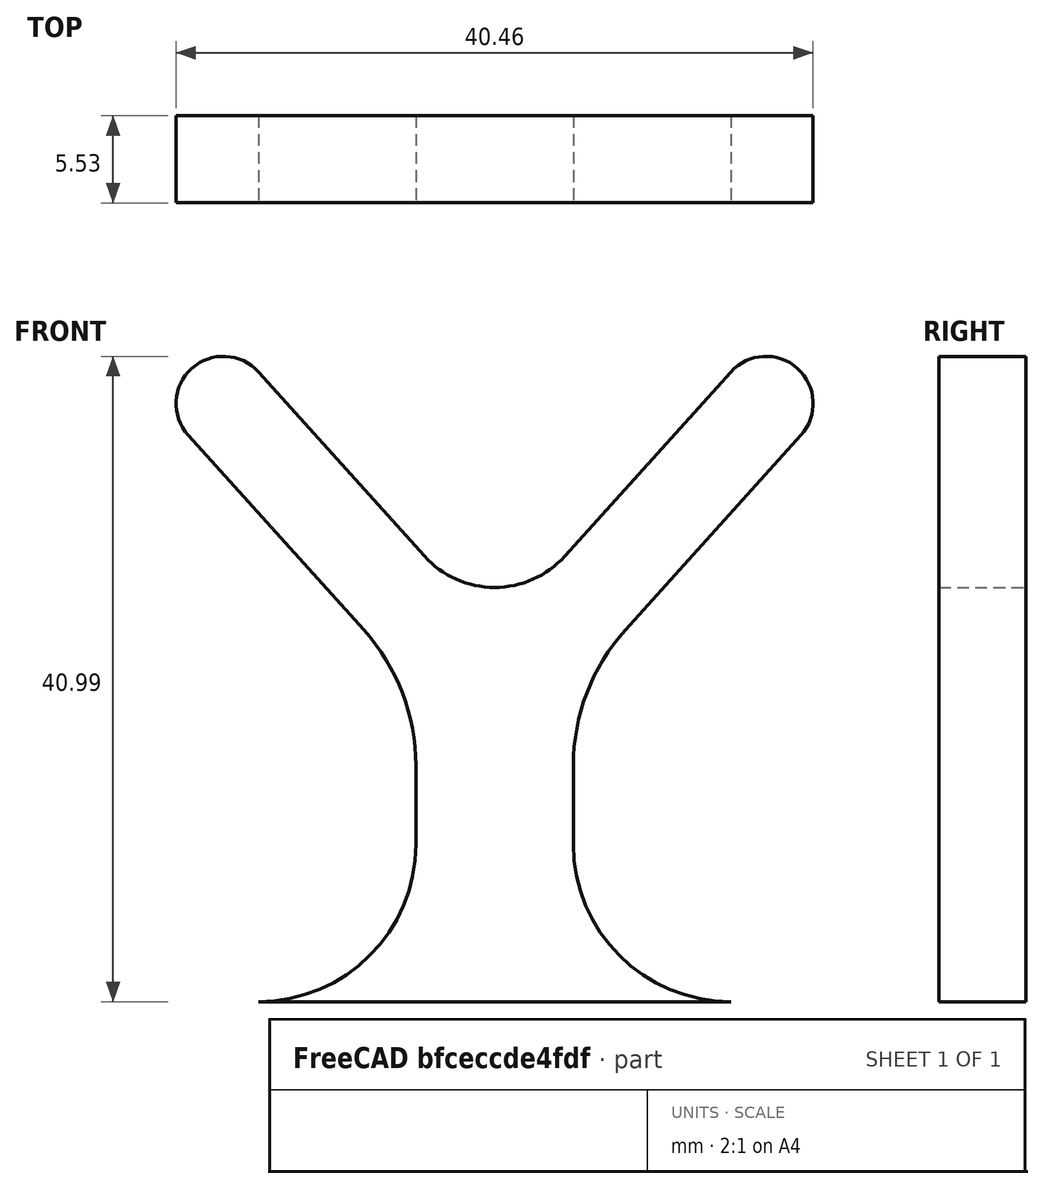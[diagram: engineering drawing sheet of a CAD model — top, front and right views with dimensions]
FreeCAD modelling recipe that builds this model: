
FCSTD DOCUMENT  (FreeCAD 0.15R4537 (Git))
Label: FrontalY_prueba
License: All rights reserved
LicenseURL: http://en.wikipedia.org/wiki/All_rights_reserved
objects: Part::Feature×3, Mesh::Feature×1, Sketcher::SketchObject×1, PartDesign::Pad×1
note: 6 computed .brp shape members not serialized (recipe doc carries the construction recipe); baked Part::Feature solids carry a one-line shape summary decoded from their .brp

FEATURE [Mesh::Feature] G004160_Cycl_marcoFrontalY
FEATURE [Part::Feature] G004160_Cycl_marcoFrontalY001
  shape: bbox 102.5 x 46.5 x 27.49 mm, 3139 faces, 0 solids (baked)
FEATURE [Part::Feature] G004160_Cycl_marcoFrontalY001001  label="G004160_Cycl_marcoFrontalY002"
  shape: bbox 102.5 x 46.5 x 27.49 mm, 1152 faces, 0 solids (baked)
FEATURE [Part::Feature] G004160_Cycl_marcoFrontalY001002  label="G004160_Cycl_marcoFrontalY003"
  shape: bbox 102.5 x 46.5 x 27.49 mm, 1152 faces, 0 solids (baked)
FEATURE [Sketcher::SketchObject] Sketch001
  Placement = pos=(0,23.6286,0) rot=(0,0.707107,0.707107;3.14159rad)
  Support = -> G004160_Cycl_marcoFrontalY001001 [Face631]
  sketch-geometry (19):
    g0: LineSegment StartX=-4.26163 StartY=11 StartZ=0 EndX=25.7384 EndY=11 EndZ=0
    g1: ArcOfCircle CenterX=-4.26164 CenterY=21 CenterZ=0 NormalX=0 NormalY=0 NormalZ=1 Radius=10 StartAngle=4.71239 EndAngle=6.28319
    g2: ArcOfCircle CenterX=25.7384 CenterY=21 CenterZ=0 NormalX=0 NormalY=0 NormalZ=1 Radius=10 StartAngle=3.14159 EndAngle=4.71239
    g3: LineSegment StartX=5.73836 StartY=21 StartZ=0 EndX=5.73836 EndY=26 EndZ=0
    g4: LineSegment StartX=15.7384 StartY=21 StartZ=0 EndX=15.7384 EndY=26 EndZ=0
    g5: LineSegment [constr] StartX=5.73836 StartY=21 StartZ=0 EndX=15.7384 EndY=21 EndZ=0
    g6: ArcOfCircle CenterX=-7.11477 CenterY=26 CenterZ=0 NormalX=0 NormalY=0 NormalZ=1 Radius=12.8531 StartAngle=6.28319 EndAngle=7.0165
    g7: ArcOfCircle CenterX=28.5915 CenterY=26 CenterZ=0 NormalX=0 NormalY=0 NormalZ=1 Radius=12.8531 StartAngle=2.40828 EndAngle=3.14159
    g8: LineSegment [constr] StartX=-4.26163 StartY=41 StartZ=0 EndX=-4.26163 EndY=11 EndZ=0
    g9: LineSegment [constr] StartX=25.7384 StartY=41 StartZ=0 EndX=25.7384 EndY=11 EndZ=0
    g10: ArcOfCircle CenterX=-6.49052 CenterY=48.992 CenterZ=0 NormalX=0 NormalY=0 NormalZ=1 Radius=3 StartAngle=0.733309 EndAngle=3.8749
    g11: ArcOfCircle CenterX=27.9673 CenterY=48.992 CenterZ=0 NormalX=0 NormalY=0 NormalZ=1 Radius=3 StartAngle=5.54988 EndAngle=8.69147
    g12: LineSegment [constr] StartX=-4.26163 StartY=51 StartZ=0 EndX=-4.26163 EndY=41 EndZ=0
    g13: LineSegment [constr] StartX=25.7384 StartY=51 StartZ=0 EndX=25.7384 EndY=41 EndZ=0
    g14: LineSegment StartX=-8.71941 StartY=46.984 StartZ=0 EndX=2.43463 EndY=34.603 EndZ=0
    g15: LineSegment StartX=19.0421 StartY=34.603 StartZ=0 EndX=30.1962 EndY=46.984 EndZ=0
    g16: LineSegment StartX=-4.26163 StartY=51 StartZ=0 EndX=6.28059 EndY=39.2981 EndZ=0
    g17: LineSegment StartX=25.7384 StartY=51 StartZ=0 EndX=15.1961 EndY=39.2981 EndZ=0
    g18: ArcOfCircle CenterX=10.7384 CenterY=43.3141 CenterZ=0 NormalX=0 NormalY=0 NormalZ=1 Radius=6 StartAngle=3.87491 EndAngle=5.54987
  constraints (60):
    c: Horizontal(g0)
    c: DistanceX(g0) = 30
    c: Coincident(g1,g0)
    c: Coincident(g2,g0)
    c: Radius(g1) = 10
    c: Equal(g1,g2)
    c: Coincident(g3,g1)
    c: Vertical(g3)
    c: Coincident(g4,g2)
    c: Vertical(g4)
    c: Tangent(g4,g2)
    c: Coincident(g5,g1)
    c: Coincident(g5,g2)
    c: Horizontal(g5)
    c: DistanceX(g5) = 10
    c: Equal(g4,g3)
    c: Coincident(g6,g3)
    c: Tangent(g6,g3)
    c: Coincident(g7,g4)
    c: Tangent(g7,g4)
    c: Coincident(g8,g0)
    c: Vertical(g8)
    c: Coincident(g9,g0)
    c: Vertical(g9)
    c: Coincident(g12,g10)
    c: Vertical(g12)
    c: Coincident(g13,g11)
    c: Vertical(g13)
    c: Coincident(g8,g12)
    c: DistanceY(g12) = -10
    c: DistanceY(g8) = -30
    c: Equal(g9,g8)
    c: Coincident(g14,g10)
    c: Coincident(g14,g6)
    c: Tangent(g6,g14)
    c: Coincident(g9,g13)
    c: Equal(g13,g12)
    c: Coincident(g15,g7)
    c: Coincident(g15,g11)
    c: Equal(g15,g14)
    c: Tangent(g7,g15)
    c: Equal(g11,g10)
    c: Tangent(g15,g11)
    c: Tangent(g14,g10)
    c: DistanceY(g4) = 5
    c: Coincident(g16,g10)
    c: Coincident(g17,g11)
    c: DistanceY(g-1,g0) = 11
    c: Tangent(g1,g0)
    c: DistanceX(g-1,g0) = -4.26163
    c: Tangent(g10,g16)
    c: Tangent(g17,g11)
    c: Parallel(g17,g15)
    c: Parallel(g16,g14)
    c: Coincident(g18,g16)
    c: Coincident(g18,g17)
    c: Tangent(g18,g17)
    c: Tangent(g18,g16)
    c: Radius(g18) = 6
    c: Radius(g10) = 3
FEATURE [PartDesign::Pad] Pad
  Length = 5.5252
  Length2 = 100
  Reversed = true
  Sketch = -> Sketch001
  Type = 0
